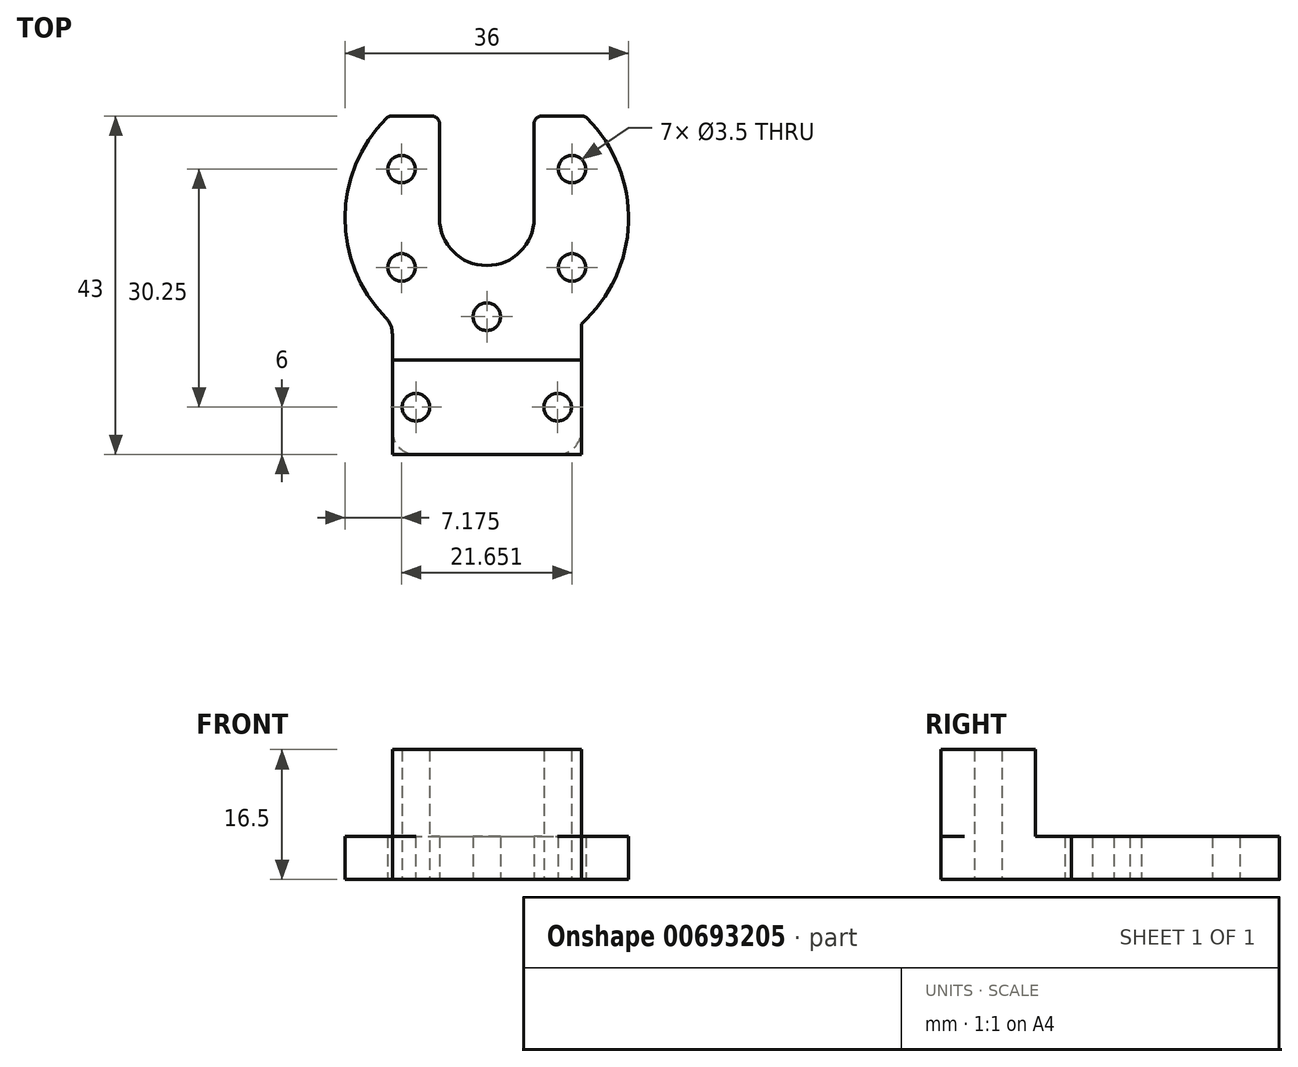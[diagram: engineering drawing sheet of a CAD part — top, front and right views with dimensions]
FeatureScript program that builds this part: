
annotation { "Feature Type Name" : "Feature", "Feature Type Description" : "" }
export const myFeature = defineFeature(function(context is Context, id is Id, definition is map)
    precondition{}
    {
        {
            var Q0;
            Q0=qCreatedBy(makeId("Top.planeOp"),FACE);
            var sketch = newSketch(context, id + "F0", { "sketchPlane" : qUnion([Q0])});
            skArc(sketch, "E0", {"start": v(-12.75, 12.7) * mm, "mid": v(0, -18) * mm, "end": v(12.75, 12.7) * mm});
            skArc(sketch, "E1", {"start": v(-6, 0) * mm, "mid": v(0, -6) * mm, "end": v(6, 0) * mm});
            skCircle(sketch, "E2", {"center": v(0, -12.5) * mm, "radius": 1.75 * mm});
            skCircle(sketch, "E3", {"center": v(10.83, 6.25) * mm, "radius": 1.75 * mm});
            skCircle(sketch, "E4", {"center": v(10.83, -6.25) * mm, "radius": 1.75 * mm});
            skCircle(sketch, "E5", {"center": v(-10.83, 6.25) * mm, "radius": 1.75 * mm});
            skCircle(sketch, "E6", {"center": v(-10.83, -6.25) * mm, "radius": 1.75 * mm});
            skLineSegment(sketch, "E7", {"start": v(-12.04, 13) * mm, "end": v(-7, 13) * mm});
            skLineSegment(sketch, "E8", {"start": v(6, 0) * mm, "end": v(6, 12) * mm});
            skLineSegment(sketch, "E9", {"start": v(-6, 0) * mm, "end": v(-6, 12) * mm});
            skLineSegment(sketch, "E10.trimOffspring", {"start": v(7, 13) * mm, "end": v(12.04, 13) * mm});
            skPoint(sketch, "E11.visualSharp", {"position": v(-6, 13) * mm});
            skArc(sketch, "E11.filletArc", {"start": v(-6, 12) * mm, "mid": v(-6.3, 12.7) * mm, "end": v(-7, 13) * mm});
            skPoint(sketch, "E12.visualSharp", {"position": v(6, 13) * mm});
            skArc(sketch, "E12.filletArc", {"start": v(7, 13) * mm, "mid": v(6.3, 12.7) * mm, "end": v(6, 12) * mm});
            skPoint(sketch, "E13.visualSharp", {"position": v(12.45, 13) * mm});
            skArc(sketch, "E13.filletArc", {"start": v(12.75, 12.7) * mm, "mid": v(12.43, 12.92) * mm, "end": v(12.04, 13) * mm});
            skPoint(sketch, "E14.visualSharp", {"position": v(-12.45, 13) * mm});
            skArc(sketch, "E14.filletArc", {"start": v(-12.04, 13) * mm, "mid": v(-12.43, 12.92) * mm, "end": v(-12.75, 12.7) * mm});
            skPoint(sketch, "E15.end.orphan", {"position": v(-8, 13) * mm});
            skPoint(sketch, "E16.start.orphan", {"position": v(-8, 0) * mm});
            skPoint(sketch, "E17.end.orphan", {"position": v(8, 13) * mm});
            skPoint(sketch, "E17.start.orphan", {"position": v(8, 0) * mm});
            skSolve(sketch);
        }
        {
            var Q0;
            Q0=qCreatedBy(makeId("Top.planeOp"),FACE);
            var sketch = newSketch(context, id + "F1", { "sketchPlane" : qUnion([Q0])});
            skArc(sketch, "E18.0", {"start": v(-12.75, 12.7) * mm, "mid": v(0, -18) * mm, "end": v(12.75, 12.7) * mm});
            skLineSegment(sketch, "E19.bottom", {"start": v(12, -30) * mm, "end": v(-12, -30) * mm});
            skLineSegment(sketch, "E19.left", {"start": v(12, -30) * mm, "end": v(12, -13.42) * mm});
            skLineSegment(sketch, "E19.right", {"start": v(-12, -30) * mm, "end": v(-12, -13.42) * mm});
            skPoint(sketch, "E19.middle", {"position": v(0, -18) * mm});
            skLineSegment(sketch, "E20", {"start": v(-12, -18) * mm, "end": v(12, -18) * mm});
            skPoint(sketch, "E21.orphan", {"position": v(12, -6) * mm});
            skPoint(sketch, "E22.orphan", {"position": v(-12, -6) * mm});
            skCircle(sketch, "E23", {"center": v(-9, -24) * mm, "radius": 1.75 * mm});
            skCircle(sketch, "E24", {"center": v(9, -24) * mm, "radius": 1.75 * mm});
            skSolve(sketch);
        }
        {
            var Q0;
            Q0=makeQuery(id+"F0.imprint","IMPRINT",FACE,{"disambiguationData":[TD([[makeQuery(id+"F0.imprint","IMPRINT",EDGE,{"derivedFrom":sQuery(id+"F0.wireOp",EDGE,"E0")}),1.0]])]});
            extrude(context, id + "F2", {"entities" : qUnion([Q0]), "depth" : 5.5 * mm, "offsetDistance" : 25 * mm});
        }
        {
            var Q0;
            {var subQ1=sQuery(id+"F1.wireOp",EDGE,"E19.bottom");Q0=makeQuery(id+"F1.imprint","IMPRINT",FACE,{"disambiguationData":[TD([[makeQuery(id+"F1.imprint","IMPRINT",EDGE,{"derivedFrom":subQ1}),-1.0]])]});}
            var Q1;
            {var subQ0=sQuery(id+"F1.wireOp",EDGE,"E19.left");var subQ1=sQuery(id+"F1.wireOp",EDGE,"E18.0");var subQ2=makeQuery(id+"F1.imprint","INTERSECT",VERTEX,{"derivedFrom":[subQ1,subQ0]});Q1=makeQuery(id+"F1.imprint","IMPRINT",FACE,{"disambiguationData":[TD([[makeQuery(id+"F1.imprint","IMPRINT",EDGE,{"disambiguationData":[TD([[subQ2,1.0]])],"derivedFrom":subQ1}),-1.0]])]});}
            var Q2;
            {var subQ0=sQuery(id+"F1.wireOp",EDGE,"E19.right");var subQ1=sQuery(id+"F1.wireOp",EDGE,"E18.0");var subQ2=makeQuery(id+"F1.imprint","INTERSECT",VERTEX,{"derivedFrom":[subQ1,subQ0]});Q2=makeQuery(id+"F1.imprint","IMPRINT",FACE,{"disambiguationData":[TD([[makeQuery(id+"F1.imprint","IMPRINT",EDGE,{"disambiguationData":[TD([[subQ2,-1.0]])],"derivedFrom":subQ1}),-1.0]])]});}
            extrude(context, id + "F3", {"entities" : qUnion([Q0, Q1, Q2]), "operationType" : NewBodyOperationType.ADD, "depth" : 5.5 * mm, "offsetDistance" : 25 * mm});
        }
        {
            var Q0;
            Q0=makeQuery(id+"F3.opExtrude","SWEPT_EDGE",EDGE,{"disambiguationData":[OSD([sQuery(id+"F1.wireOp",EDGE,"E18.0"),sQuery(id+"F1.wireOp",EDGE,"E19.right")])]});
            var Q1;
            Q1=makeQuery(id+"F3.opExtrude","SWEPT_EDGE",EDGE,{"disambiguationData":[OSD([sQuery(id+"F1.wireOp",EDGE,"E19.bottom"),sQuery(id+"F1.wireOp",EDGE,"E19.right")])]});
            var Q2;
            Q2=makeQuery(id+"F3.opExtrude","SWEPT_EDGE",EDGE,{"disambiguationData":[OSD([sQuery(id+"F1.wireOp",EDGE,"E18.0"),sQuery(id+"F1.wireOp",EDGE,"E19.left")])]});
            var Q3;
            Q3=makeQuery(id+"F3.opExtrude","SWEPT_EDGE",EDGE,{"disambiguationData":[OSD([sQuery(id+"F1.wireOp",EDGE,"E19.bottom"),sQuery(id+"F1.wireOp",EDGE,"E19.left")])]});
            fillet(context, id + "F4", {"entities" : qUnion([Q0, Q1, Q2, Q3]), "radius" : 3 * mm, "tangentPropagation" : true, "allowEdgeOverflow" : false});
        }
        {
            var Q0;
            Q0=makeQuery(id+"F3.boolean.opBoolean","MERGE",FACE,{"derivedFrom":[makeQuery(id+"F2.opExtrude","CAP_FACE",FACE,{"disambiguationData":[OSD([sQuery(id+"F0.wireOp",EDGE,"E0"),sQuery(id+"F0.wireOp",EDGE,"E1"),sQuery(id+"F0.wireOp",EDGE,"E2"),sQuery(id+"F0.wireOp",EDGE,"E3"),sQuery(id+"F0.wireOp",EDGE,"E4"),sQuery(id+"F0.wireOp",EDGE,"E5"),sQuery(id+"F0.wireOp",EDGE,"E6"),sQuery(id+"F0.wireOp",EDGE,"E7"),sQuery(id+"F0.wireOp",EDGE,"E8"),sQuery(id+"F0.wireOp",EDGE,"E9"),sQuery(id+"F0.wireOp",EDGE,"E10.trimOffspring"),sQuery(id+"F0.wireOp",EDGE,"E11.filletArc"),sQuery(id+"F0.wireOp",EDGE,"E12.filletArc"),sQuery(id+"F0.wireOp",EDGE,"E13.filletArc"),sQuery(id+"F0.wireOp",EDGE,"E14.filletArc")])],"isStart":false}),makeQuery(id+"F3.opExtrude","CAP_FACE",FACE,{"disambiguationData":[OSD([sQuery(id+"F1.wireOp",EDGE,"E18.0"),sQuery(id+"F1.wireOp",EDGE,"E19.bottom"),sQuery(id+"F1.wireOp",EDGE,"E19.left"),sQuery(id+"F1.wireOp",EDGE,"E19.right"),sQuery(id+"F1.wireOp",EDGE,"E23"),sQuery(id+"F1.wireOp",EDGE,"E24")])],"isStart":false})]});
            var sketch = newSketch(context, id + "F5", { "sketchPlane" : qUnion([Q0])});
            skLineSegment(sketch, "E25.0", {"start": v(-12, -18) * mm, "end": v(12, -18) * mm});
            skCircle(sketch, "E26.0", {"center": v(9, -24) * mm, "radius": 1.75 * mm});
            skCircle(sketch, "E26.1", {"center": v(-9, -24) * mm, "radius": 1.75 * mm});
            skLineSegment(sketch, "E26.2", {"start": v(-12, -30) * mm, "end": v(-12, -18) * mm});
            skLineSegment(sketch, "E26.3", {"start": v(12, -30) * mm, "end": v(-12, -30) * mm});
            skLineSegment(sketch, "E26.4", {"start": v(12, -30) * mm, "end": v(12, -18) * mm});
            skPoint(sketch, "E27.orphan", {"position": v(12, -13.42) * mm});
            skPoint(sketch, "E28.orphan", {"position": v(-12, -13.42) * mm});
            skSolve(sketch);
        }
        {
            var Q0;
            Q0 = qSketchRegion(id + "F5", true);
            extrude(context, id + "F6", {"entities" : qUnion([Q0]), "operationType" : NewBodyOperationType.ADD, "depth" : 11 * mm, "offsetDistance" : 25 * mm});
        }
    });
